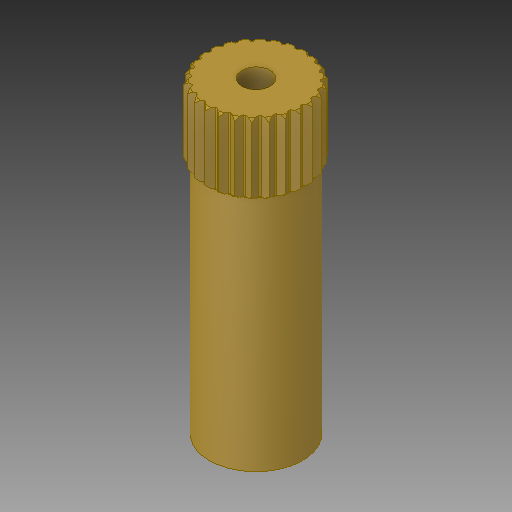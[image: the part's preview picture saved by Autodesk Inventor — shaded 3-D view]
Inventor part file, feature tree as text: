
AUTODESK INVENTOR PART (.ipt)
format: ipt  version: 2017 (Build 210142000, 142)  size: 283,136 bytes
history: native  units: in
note: dims shown in document units (in); Inventor stores cm internally (conversion verified against a paired STEP export)
features: mirror x1
ambient origin geometry x8: Origin, YZ Plane, XZ Plane, XY Plane, X Axis, Y Axis, Z Axis, Center Point
bodies: Solid1 (feature_tree)
feature tree (1):
  mirror  "Mirror1"
